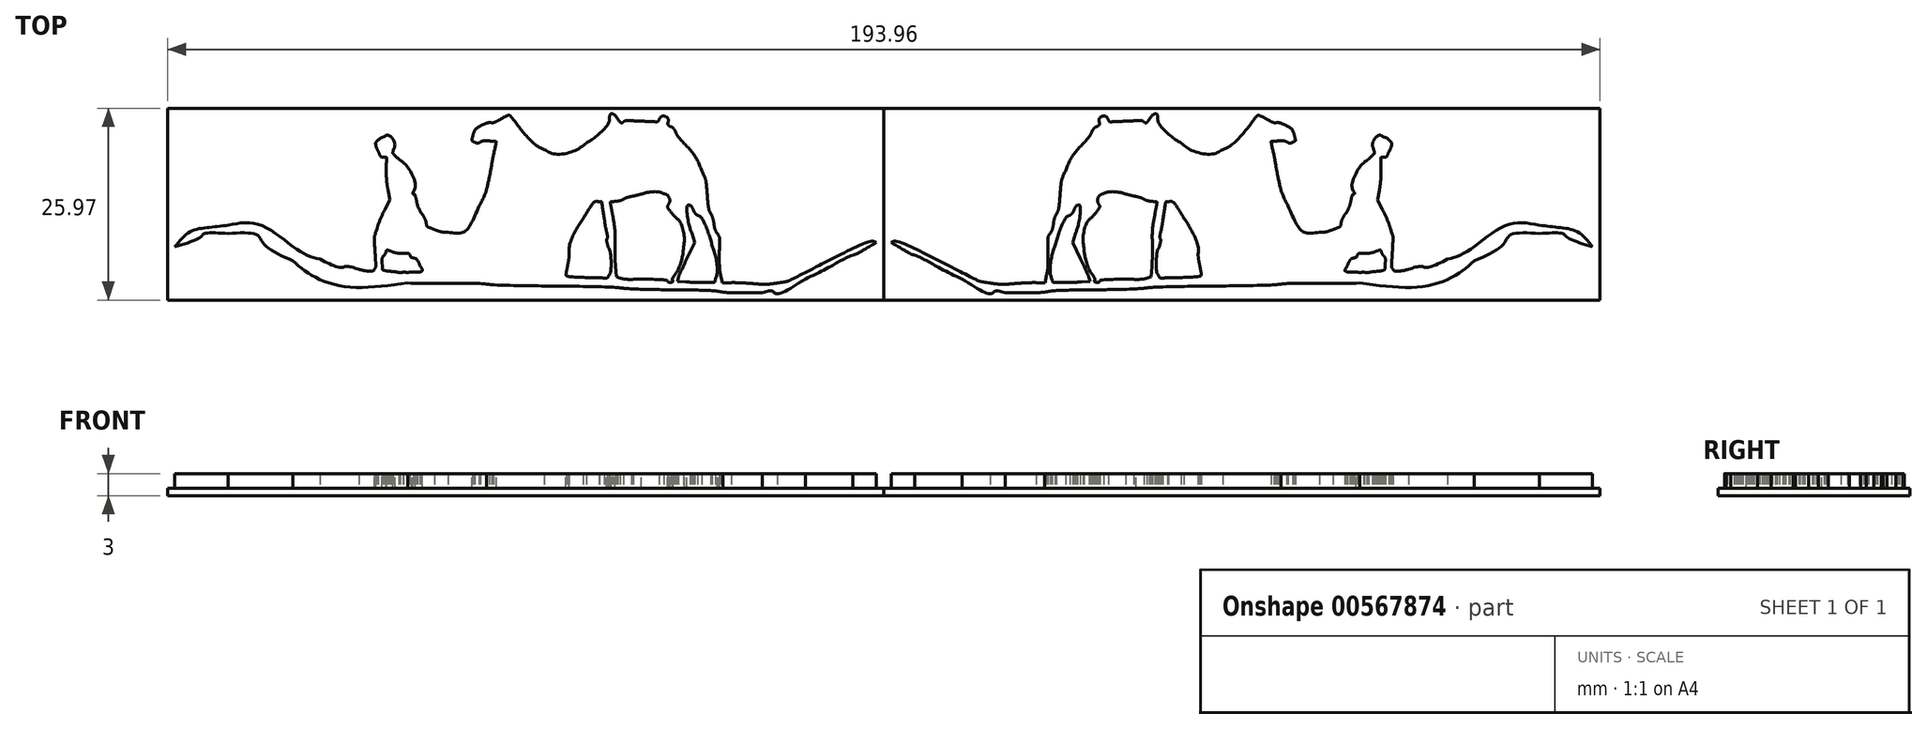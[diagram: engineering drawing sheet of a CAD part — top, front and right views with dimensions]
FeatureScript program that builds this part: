
annotation { "Feature Type Name" : "Feature", "Feature Type Description" : "" }
export const myFeature = defineFeature(function(context is Context, id is Id, definition is map)
    precondition{}
    {
        {
            var Q0;
            Q0=qCreatedBy(makeId("Top.planeOp"),FACE);
            var sketch = newSketch(context, id + "F0", { "sketchPlane" : qUnion([Q0])});
            skPoint(sketch, "E0.middle", {"position": v(0, 0) * mm});
            skFitSpline(sketch, "E1", {"points": [v(26.7, -11.93) * mm, v(25.66, -11.75) * mm, v(23.58, -11.65) * mm, v(20.02, -11.6) * mm]});
            skFitSpline(sketch, "E2", {"points": [v(20.02, -11.6) * mm, v(17.17, -11.57) * mm, v(14.02, -11.46) * mm, v(13, -11.36) * mm]});
            skFitSpline(sketch, "E3", {"points": [v(13, -11.36) * mm, v(12, -11.27) * mm, v(7.87, -11.15) * mm, v(3.83, -11.1) * mm]});
            skFitSpline(sketch, "E4", {"points": [v(3.83, -11.1) * mm, v(-0.2, -11.05) * mm, v(-4.31, -10.93) * mm, v(-5.3, -10.84) * mm]});
            skFitSpline(sketch, "E5", {"points": [v(-5.3, -10.84) * mm, v(-6.28, -10.75) * mm, v(-11.08, -10.75) * mm, v(-15.97, -10.7) * mm]});
            skFitSpline(sketch, "E6", {"points": [v(-15.97, -10.7) * mm, v(-24.16, -11.2) * mm, v(-28.99, -9.62) * mm, v(-31.48, -7.69) * mm]});
            skFitSpline(sketch, "E7", {"points": [v(-31.48, -7.69) * mm, v(-35.44, -5.43) * mm, v(-36.3, -4.22) * mm, v(-40.29, -4) * mm]});
            skFitSpline(sketch, "E8", {"points": [v(-40.29, -4) * mm, v(-43.5, -4.01) * mm, v(-44.02, -4.46) * mm, v(-47.5, -5.8) * mm]});
            skFitSpline(sketch, "E9", {"points": [v(-47.5, -5.8) * mm, v(-45.49, -3.77) * mm, v(-43.1, -3.18) * mm, v(-40.24, -2.86) * mm]});
            skFitSpline(sketch, "E10", {"points": [v(-40.24, -2.86) * mm, v(-35.9, -2.82) * mm, v(-30.7, -6.32) * mm, v(-27.85, -7.45) * mm]});
            skFitSpline(sketch, "E11", {"points": [v(-27.85, -7.45) * mm, v(-25.01, -8.6) * mm, v(-24.29, -8.43) * mm, v(-22.55, -8.84) * mm]});
            skFitSpline(sketch, "E12", {"points": [v(-22.55, -8.84) * mm, v(-22.19, -8.93) * mm, v(-20.69, -9.05) * mm, v(-20.45, -8.77) * mm]});
            skFitSpline(sketch, "E13", {"points": [v(-20.45, -8.77) * mm, v(-20.31, -8.6) * mm, v(-20.29, -7.98) * mm, v(-20.37, -6.51) * mm]});
            skFitSpline(sketch, "E14", {"points": [v(-20.37, -6.51) * mm, v(-20.48, -4.67) * mm, v(-20.46, -4.39) * mm, v(-20.1, -3.3) * mm]});
            skFitSpline(sketch, "E15", {"points": [v(-20.1, -3.3) * mm, v(-19.9, -2.63) * mm, v(-19.42, -1.49) * mm, v(-19.05, -0.76) * mm]});
            skFitSpline(sketch, "E16", {"points": [v(-18.62, 1.91) * mm, v(-18.75, 2.65) * mm, v(-18.85, 3.95) * mm, v(-18.84, 4.8) * mm]});
            skFitSpline(sketch, "E17", {"points": [v(-18.84, 4.8) * mm, v(-18.83, 6.29) * mm, v(-18.84, 6.34) * mm, v(-19.2, 6.34) * mm]});
            skFitSpline(sketch, "E18", {"points": [v(-19.2, 6.34) * mm, v(-19.48, 6.34) * mm, v(-19.66, 6.53) * mm, v(-19.93, 7.09) * mm]});
            skFitSpline(sketch, "E19", {"points": [v(-19.93, 7.09) * mm, v(-20.12, 7.5) * mm, v(-20.28, 7.94) * mm, v(-20.28, 8.06) * mm]});
            skFitSpline(sketch, "E20", {"points": [v(-20.28, 8.06) * mm, v(-20.28, 8.32) * mm, v(-19.66, 8.91) * mm, v(-19.22, 9.07) * mm]});
            skFitSpline(sketch, "E21", {"points": [v(-19.22, 9.07) * mm, v(-18.52, 9.31) * mm, v(-17.71, 8.24) * mm, v(-17.9, 7.3) * mm]});
            skFitSpline(sketch, "E22", {"points": [v(-17.9, 7.3) * mm, v(-17.96, 6.93) * mm, v(-17.84, 6.73) * mm, v(-17.15, 6.1) * mm]});
            skFitSpline(sketch, "E23", {"points": [v(-17.15, 6.1) * mm, v(-15.99, 5.03) * mm, v(-14.9, 2.56) * mm, v(-15.2, 1.65) * mm]});
            skFitSpline(sketch, "E24", {"points": [v(-15.2, 1.65) * mm, v(-15.25, 1.48) * mm, v(-15.22, 1.33) * mm, v(-15.13, 1.33) * mm]});
            skFitSpline(sketch, "E25", {"points": [v(-15.13, 1.33) * mm, v(-15.04, 1.33) * mm, v(-14.87, 0.91) * mm, v(-14.75, 0.4) * mm]});
            skFitSpline(sketch, "E26", {"points": [v(-14.75, 0.4) * mm, v(-14.64, -0.12) * mm, v(-14.32, -0.87) * mm, v(-14.05, -1.28) * mm]});
            skFitSpline(sketch, "E27", {"points": [v(-14.05, -1.28) * mm, v(-13.78, -1.7) * mm, v(-13.5, -2.26) * mm, v(-13.45, -2.54) * mm]});
            skFitSpline(sketch, "E28", {"points": [v(-13.45, -2.54) * mm, v(-13.36, -2.99) * mm, v(-13.2, -3.1) * mm, v(-12.35, -3.44) * mm]});
            skFitSpline(sketch, "E29", {"points": [v(-12.35, -3.44) * mm, v(-11.8, -3.65) * mm, v(-10.97, -3.83) * mm, v(-10.5, -3.83) * mm]});
            skFitSpline(sketch, "E30", {"points": [v(-10.5, -3.83) * mm, v(-8.53, -3.85) * mm, v(-7.65, -3.1) * mm, v(-6.27, -0.25) * mm]});
            skFitSpline(sketch, "E31", {"points": [v(-6.27, -0.25) * mm, v(-5.48, 1.37) * mm, v(-5.21, 2.24) * mm, v(-4.91, 3.65) * mm]});
            skFitSpline(sketch, "E32", {"points": [v(-4.91, 3.65) * mm, v(-4.7, 4.7) * mm, v(-4.46, 6.1) * mm, v(-4.33, 6.7) * mm]});
            skFitSpline(sketch, "E33", {"points": [v(-4.33, 6.7) * mm, v(-3.96, 8.44) * mm, v(-3.97, 8.46) * mm, v(-4.89, 8.55) * mm]});
            skFitSpline(sketch, "E34", {"points": [v(-4.89, 8.55) * mm, v(-5.33, 8.59) * mm, v(-5.86, 8.53) * mm, v(-6.09, 8.42) * mm]});
            skFitSpline(sketch, "E35", {"points": [v(-6.09, 8.42) * mm, v(-6.39, 8.27) * mm, v(-6.6, 8.26) * mm, v(-6.89, 8.4) * mm]});
            skFitSpline(sketch, "E36", {"points": [v(-6.89, 8.4) * mm, v(-7.21, 8.54) * mm, v(-7.26, 8.65) * mm, v(-7.17, 9.08) * mm]});
            skFitSpline(sketch, "E37", {"points": [v(-7.17, 9.08) * mm, v(-7.1, 9.36) * mm, v(-7, 9.7) * mm, v(-6.92, 9.85) * mm]});
            skFitSpline(sketch, "E38", {"points": [v(-6.92, 9.85) * mm, v(-6.76, 10.17) * mm, v(-5.08, 11.01) * mm, v(-4.6, 11.01) * mm]});
            skFitSpline(sketch, "E39", {"points": [v(-4.6, 11.01) * mm, v(-4.42, 11.01) * mm, v(-3.98, 11.16) * mm, v(-3.64, 11.34) * mm]});
            skFitSpline(sketch, "E40", {"points": [v(-3.64, 11.34) * mm, v(-2.3, 12.04) * mm, v(-2.12, 11.98) * mm, v(-1.03, 10.64) * mm]});
            skFitSpline(sketch, "E41", {"points": [v(-1.03, 10.64) * mm, v(0.14, 9.19) * mm, v(1.71, 7.77) * mm, v(2.56, 7.4) * mm]});
            skFitSpline(sketch, "E42", {"points": [v(2.56, 7.4) * mm, v(3.94, 6.79) * mm, v(6.6, 7.2) * mm, v(8.23, 8.27) * mm]});
            skFitSpline(sketch, "E43", {"points": [v(8.23, 8.27) * mm, v(9.44, 9.07) * mm, v(11.26, 10.96) * mm, v(11.37, 11.55) * mm]});
            skFitSpline(sketch, "E44", {"points": [v(11.37, 11.55) * mm, v(11.5, 12.17) * mm, v(11.95, 12.15) * mm, v(12.5, 11.48) * mm]});
            skFitSpline(sketch, "E45", {"points": [v(12.5, 11.48) * mm, v(12.88, 11.04) * mm, v(13, 10.98) * mm, v(13.25, 11.14) * mm]});
            skFitSpline(sketch, "E46", {"points": [v(13.25, 11.14) * mm, v(13.46, 11.26) * mm, v(14.25, 11.3) * mm, v(15.7, 11.23) * mm]});
            skFitSpline(sketch, "E47", {"points": [v(15.7, 11.23) * mm, v(17.57, 11.14) * mm, v(17.88, 11.17) * mm, v(18.08, 11.4) * mm]});
            skFitSpline(sketch, "E48", {"points": [v(18.08, 11.4) * mm, v(18.5, 11.91) * mm, v(19.27, 11.63) * mm, v(19.27, 10.97) * mm]});
            skFitSpline(sketch, "E49", {"points": [v(19.27, 10.97) * mm, v(19.27, 10.8) * mm, v(19.44, 10.59) * mm, v(19.66, 10.5) * mm]});
            skFitSpline(sketch, "E50", {"points": [v(19.66, 10.5) * mm, v(19.88, 10.4) * mm, v(20.18, 10.05) * mm, v(20.33, 9.73) * mm]});
            skFitSpline(sketch, "E51", {"points": [v(20.33, 9.73) * mm, v(20.48, 9.42) * mm, v(20.93, 8.8) * mm, v(21.32, 8.37) * mm]});
            skFitSpline(sketch, "E52", {"points": [v(21.32, 8.37) * mm, v(22.48, 7.11) * mm, v(23.25, 5.94) * mm, v(23.86, 4.53) * mm]});
            skFitSpline(sketch, "E53", {"points": [v(23.86, 4.53) * mm, v(24.34, 3.44) * mm, v(24.46, 2.89) * mm, v(24.6, 1.26) * mm]});
            skFitSpline(sketch, "E54", {"points": [v(24.6, 1.26) * mm, v(24.72, -0.01) * mm, v(24.88, -0.9) * mm, v(25.09, -1.3) * mm]});
            skFitSpline(sketch, "E55", {"points": [v(25.09, -1.3) * mm, v(25.26, -1.64) * mm, v(25.45, -2.26) * mm, v(25.5, -2.68) * mm]});
            skFitSpline(sketch, "E56", {"points": [v(25.5, -2.68) * mm, v(25.57, -3.1) * mm, v(25.76, -3.67) * mm, v(25.94, -3.97) * mm]});
            skFitSpline(sketch, "E57", {"points": [v(25.94, -3.97) * mm, v(26.22, -4.42) * mm, v(26.26, -4.79) * mm, v(26.24, -6.55) * mm]});
            skFitSpline(sketch, "E58", {"points": [v(26.24, -6.55) * mm, v(26.23, -7.67) * mm, v(26.32, -9.05) * mm, v(26.43, -9.61) * mm]});
            skLineSegment(sketch, "E59", {"start": v(-19.05, -0.76) * mm, "end": v(-18.39, 0.58) * mm});
            skLineSegment(sketch, "E60", {"start": v(-18.39, 0.58) * mm, "end": v(-18.62, 1.91) * mm});
            skFitSpline(sketch, "E61", {"points": [v(27.84, -10.64) * mm, v(28.5, -10.64) * mm, v(29.84, -10.7) * mm, v(30.83, -10.77) * mm]});
            skFitSpline(sketch, "E62", {"points": [v(30.83, -10.77) * mm, v(32.1, -10.86) * mm, v(33.06, -10.83) * mm, v(34.08, -10.67) * mm]});
            skFitSpline(sketch, "E63", {"points": [v(34.08, -10.67) * mm, v(35.42, -10.47) * mm, v(35.87, -10.28) * mm, v(39.72, -8.33) * mm]});
            skFitSpline(sketch, "E64", {"points": [v(39.72, -8.33) * mm, v(43.61, -6.35) * mm, v(46.93, -5.02) * mm, v(47.5, -5.21) * mm]});
            skFitSpline(sketch, "E65", {"points": [v(47.5, -5.21) * mm, v(45.59, -6.32) * mm, v(44.86, -6.73) * mm, v(44.3, -6.9) * mm]});
            skFitSpline(sketch, "E66", {"points": [v(44.3, -6.9) * mm, v(42.86, -7.57) * mm, v(41.25, -8.48) * mm, v(37.87, -10.16) * mm]});
            skFitSpline(sketch, "E67", {"points": [v(37.87, -10.16) * mm, v(33.93, -12.13) * mm, v(33.41, -11.77) * mm, v(32.05, -12) * mm]});
            skFitSpline(sketch, "E68", {"points": [v(32.05, -12) * mm, v(30.61, -12) * mm, v(27.7, -12) * mm, v(26.7, -11.93) * mm]});
            skLineSegment(sketch, "E69", {"start": v(26.43, -9.61) * mm, "end": v(26.64, -10.64) * mm});
            skLineSegment(sketch, "E70", {"start": v(26.64, -10.64) * mm, "end": v(27.84, -10.64) * mm});
            skFitSpline(sketch, "E71", {"points": [v(25.68, -10.26) * mm, v(25.94, -9.3) * mm, v(25.76, -7.18) * mm, v(25.29, -5.63) * mm]});
            skFitSpline(sketch, "E72", {"points": [v(25.29, -5.63) * mm, v(24.71, -3.77) * mm, v(23.74, -1.75) * mm, v(23.3, -1.52) * mm]});
            skFitSpline(sketch, "E73", {"points": [v(23.3, -1.52) * mm, v(23.12, -1.42) * mm, v(22.86, -1.08) * mm, v(22.7, -0.76) * mm]});
            skFitSpline(sketch, "E74", {"points": [v(22.7, -0.76) * mm, v(22.55, -0.43) * mm, v(22.35, -0.17) * mm, v(22.26, -0.17) * mm]});
            skFitSpline(sketch, "E75", {"points": [v(22.26, -0.17) * mm, v(21.93, -0.17) * mm, v(22.1, -2.62) * mm, v(22.5, -3.92) * mm]});
            skFitSpline(sketch, "E76", {"points": [v(21.85, -7.4) * mm, v(21.27, -8.6) * mm, v(20.74, -9.8) * mm, v(20.68, -10.05) * mm]});
            skLineSegment(sketch, "E77", {"start": v(22.5, -3.92) * mm, "end": v(22.9, -5.19) * mm});
            skLineSegment(sketch, "E78", {"start": v(22.9, -5.19) * mm, "end": v(21.85, -7.4) * mm});
            skFitSpline(sketch, "E79", {"points": [v(21.71, -10.55) * mm, v(22.34, -10.58) * mm, v(23.47, -10.6) * mm, v(24.22, -10.6) * mm]});
            skFitSpline(sketch, "E80", {"points": [v(24.22, -10.6) * mm, v(25.45, -10.6) * mm, v(25.6, -10.56) * mm, v(25.68, -10.26) * mm]});
            skLineSegment(sketch, "E81", {"start": v(20.68, -10.05) * mm, "end": v(20.57, -10.5) * mm});
            skLineSegment(sketch, "E82", {"start": v(20.57, -10.5) * mm, "end": v(21.71, -10.55) * mm});
            skFitSpline(sketch, "E83", {"points": [v(19.9, -10.3) * mm, v(19.88, -10.19) * mm, v(20, -9.9) * mm, v(20.16, -9.65) * mm]});
            skFitSpline(sketch, "E84", {"points": [v(20.16, -9.65) * mm, v(20.62, -8.95) * mm, v(21.26, -6.98) * mm, v(21.37, -5.9) * mm]});
            skFitSpline(sketch, "E85", {"points": [v(21.37, -5.9) * mm, v(21.5, -4.65) * mm, v(20.97, -2.5) * mm, v(20.4, -1.86) * mm]});
            skFitSpline(sketch, "E86", {"points": [v(20.4, -1.86) * mm, v(19.68, -1.09) * mm, v(19.23, -0.33) * mm, v(19.33, -0.08) * mm]});
            skFitSpline(sketch, "E87", {"points": [v(19.33, -0.08) * mm, v(19.54, 0.47) * mm, v(19.23, 1.2) * mm, v(18.7, 1.41) * mm]});
            skFitSpline(sketch, "E88", {"points": [v(18.7, 1.41) * mm, v(18.12, 1.64) * mm, v(16.69, 1.62) * mm, v(15.68, 1.35) * mm]});
            skFitSpline(sketch, "E89", {"points": [v(15.68, 1.35) * mm, v(15.31, 1.26) * mm, v(14.71, 1.12) * mm, v(14.34, 1.04) * mm]});
            skFitSpline(sketch, "E90", {"points": [v(14.34, 1.04) * mm, v(13.98, 0.96) * mm, v(13.5, 0.8) * mm, v(13.26, 0.67) * mm]});
            skFitSpline(sketch, "E91", {"points": [v(13.26, 0.67) * mm, v(13.04, 0.55) * mm, v(12.55, 0.41) * mm, v(12.18, 0.37) * mm]});
            skFitSpline(sketch, "E92", {"points": [v(12.18, 0.37) * mm, v(11.81, 0.33) * mm, v(11.5, 0.29) * mm, v(11.5, 0.27) * mm]});
            skFitSpline(sketch, "E93", {"points": [v(11.5, 0.27) * mm, v(11.48, 0.26) * mm, v(11.63, -0.58) * mm, v(11.8, -1.59) * mm]});
            skFitSpline(sketch, "E94", {"points": [v(11.8, -1.59) * mm, v(12.01, -2.77) * mm, v(12.12, -4.08) * mm, v(12.1, -5.26) * mm]});
            skFitSpline(sketch, "E95", {"points": [v(12.1, -5.26) * mm, v(12.1, -6.27) * mm, v(12.13, -7.7) * mm, v(12.19, -8.46) * mm]});
            skFitSpline(sketch, "E96", {"points": [v(12.85, -10.01) * mm, v(13.15, -10.11) * mm, v(13.95, -10.2) * mm, v(14.62, -10.2) * mm]});
            skFitSpline(sketch, "E97", {"points": [v(14.62, -10.2) * mm, v(16.29, -10.18) * mm, v(19.14, -10.33) * mm, v(19.24, -10.43) * mm]});
            skFitSpline(sketch, "E98", {"points": [v(19.24, -10.43) * mm, v(19.41, -10.6) * mm, v(19.95, -10.5) * mm, v(19.9, -10.3) * mm]});
            skLineSegment(sketch, "E99", {"start": v(12.19, -8.46) * mm, "end": v(12.29, -9.83) * mm});
            skLineSegment(sketch, "E100", {"start": v(12.29, -9.83) * mm, "end": v(12.85, -10.01) * mm});
            skFitSpline(sketch, "E101", {"points": [v(11.25, -9.69) * mm, v(11.5, -9.21) * mm, v(11.47, -6.48) * mm, v(11.2, -5.82) * mm]});
            skFitSpline(sketch, "E102", {"points": [v(11.2, -5.82) * mm, v(10.98, -4.84) * mm, v(11.02, -4.75) * mm, v(11.04, -4.68) * mm]});
            skFitSpline(sketch, "E103", {"points": [v(11.04, -4.68) * mm, v(11.12, -4.4) * mm, v(11.11, -4.4) * mm, v(11.08, -4.23) * mm]});
            skFitSpline(sketch, "E104", {"points": [v(11.08, -4.23) * mm, v(11.05, -4.06) * mm, v(10.83, -3.1) * mm, v(10.68, -2.09) * mm]});
            skFitSpline(sketch, "E105", {"points": [v(10.68, -2.09) * mm, v(10.34, 0.21) * mm, v(10.3, 0.33) * mm, v(9.93, 0.33) * mm]});
            skFitSpline(sketch, "E106", {"points": [v(9.93, 0.33) * mm, v(9.4, 0.33) * mm, v(8.85, -0.26) * mm, v(7.8, -1.95) * mm]});
            skFitSpline(sketch, "E107", {"points": [v(7.8, -1.95) * mm, v(6.75, -3.64) * mm, v(5.92, -5.73) * mm, v(5.91, -6.7) * mm]});
            skFitSpline(sketch, "E108", {"points": [v(5.91, -6.7) * mm, v(5.9, -7) * mm, v(5.8, -7.78) * mm, v(5.68, -8.43) * mm]});
            skFitSpline(sketch, "E109", {"points": [v(5.68, -8.43) * mm, v(5.55, -9.07) * mm, v(5.48, -9.63) * mm, v(5.52, -9.67) * mm]});
            skFitSpline(sketch, "E110", {"points": [v(5.52, -9.67) * mm, v(5.6, -9.75) * mm, v(8.38, -9.94) * mm, v(10.04, -9.99) * mm]});
            skFitSpline(sketch, "E111", {"points": [v(10.04, -9.99) * mm, v(10.91, -10) * mm, v(11.1, -9.96) * mm, v(11.25, -9.69) * mm]});
            skFitSpline(sketch, "E112", {"points": [v(0.74, -9.57) * mm, v(1.15, -9.6) * mm, v(1.58, -9.58) * mm, v(2.7, -9.62) * mm]});
            skFitSpline(sketch, "E113", {"points": [v(4.84, -9.06) * mm, v(4.9, -8.71) * mm, v(5.05, -7.9) * mm, v(5.19, -7.27) * mm]});
            skFitSpline(sketch, "E114", {"points": [v(5.19, -7.27) * mm, v(5.34, -6.54) * mm, v(5.4, -5.8) * mm, v(5.33, -5.24) * mm]});
            skFitSpline(sketch, "E115", {"points": [v(5.33, -5.24) * mm, v(5.2, -4.3) * mm, v(5.18, -4.36) * mm, v(6.4, -2.17) * mm]});
            skFitSpline(sketch, "E116", {"points": [v(6.4, -2.17) * mm, v(6.8, -1.48) * mm, v(7.26, -0.47) * mm, v(7.44, 0.07) * mm]});
            skFitSpline(sketch, "E117", {"points": [v(7.44, 0.07) * mm, v(7.76, 1.02) * mm, v(7.77, 1.09) * mm, v(7.5, 1.8) * mm]});
            skFitSpline(sketch, "E118", {"points": [v(7.5, 1.8) * mm, v(7.16, 2.67) * mm, v(6.43, 3.5) * mm, v(6, 3.5) * mm]});
            skFitSpline(sketch, "E119", {"points": [v(6, 3.5) * mm, v(5.33, 3.5) * mm, v(2.98, 4.07) * mm, v(2.18, 4.42) * mm]});
            skFitSpline(sketch, "E120", {"points": [v(2.18, 4.42) * mm, v(1.33, 4.8) * mm, v(0.1, 5.72) * mm, v(-1.5, 7.2) * mm]});
            skFitSpline(sketch, "E121", {"points": [v(-1.5, 7.2) * mm, v(-1.97, 7.63) * mm, v(-2.65, 8.16) * mm, v(-3.05, 8.23) * mm]});
            skFitSpline(sketch, "E122", {"points": [v(-3.05, 8.23) * mm, v(-3.31, 8.27) * mm, v(-3.27, 8.2) * mm, v(-3.57, 6.6) * mm]});
            skFitSpline(sketch, "E123", {"points": [v(-3.57, 6.6) * mm, v(-4.3, 2.7) * mm, v(-4.8, 1.08) * mm, v(-5.7, -0.73) * mm]});
            skFitSpline(sketch, "E124", {"points": [v(-5.7, -0.73) * mm, v(-6.25, -1.87) * mm, v(-7.06, -3.25) * mm, v(-7.5, -3.57) * mm]});
            skFitSpline(sketch, "E125", {"points": [v(-7.5, -3.57) * mm, v(-8.01, -4.03) * mm, v(-8.87, -4.46) * mm, v(-9.48, -4.54) * mm]});
            skFitSpline(sketch, "E126", {"points": [v(-9.48, -4.54) * mm, v(-10.05, -4.71) * mm, v(-11.8, -4.36) * mm, v(-12.09, -4.31) * mm]});
            skFitSpline(sketch, "E127", {"points": [v(-12.09, -4.31) * mm, v(-12.85, -4.14) * mm, v(-12.68, -4.7) * mm, v(-12.47, -4.95) * mm]});
            skFitSpline(sketch, "E128", {"points": [v(-12.47, -4.95) * mm, v(-12.02, -5.07) * mm, v(-11.7, -5.65) * mm, v(-11.94, -5.93) * mm]});
            skFitSpline(sketch, "E129", {"points": [v(-11.94, -5.93) * mm, v(-12.08, -6.1) * mm, v(-12.08, -6.25) * mm, v(-11.93, -6.51) * mm]});
            skFitSpline(sketch, "E130", {"points": [v(-11.93, -6.51) * mm, v(-11.52, -7.3) * mm, v(-12.2, -7.6) * mm, v(-13.12, -7.06) * mm]});
            skFitSpline(sketch, "E131", {"points": [v(-13.12, -7.06) * mm, v(-13.58, -6.79) * mm, v(-13.62, -6.79) * mm, v(-13.89, -7.05) * mm]});
            skFitSpline(sketch, "E132", {"points": [v(-13.89, -7.05) * mm, v(-13.97, -7.24) * mm, v(-13.95, -7.4) * mm, v(-13.9, -7.53) * mm]});
            skFitSpline(sketch, "E133", {"points": [v(-13.9, -7.53) * mm, v(-13.75, -7.86) * mm, v(-13.47, -8.1) * mm, v(-13.2, -8.45) * mm]});
            skFitSpline(sketch, "E134", {"points": [v(-13.2, -8.45) * mm, v(-12.86, -8.97) * mm, v(-12.6, -9.17) * mm, v(-12.16, -9.25) * mm]});
            skFitSpline(sketch, "E135", {"points": [v(-12.16, -9.25) * mm, v(-11.84, -9.32) * mm, v(-9.1, -9.4) * mm, v(-6.05, -9.44) * mm]});
            skFitSpline(sketch, "E136", {"points": [v(-6.05, -9.44) * mm, v(-3.02, -9.48) * mm, v(-0.7, -9.52) * mm, v(-0.46, -9.55) * mm]});
            skFitSpline(sketch, "E137", {"points": [v(-0.46, -9.55) * mm, v(-0.08, -9.58) * mm, v(0.25, -9.55) * mm, v(0.74, -9.57) * mm]});
            skLineSegment(sketch, "E138", {"start": v(2.7, -9.62) * mm, "end": v(4.73, -9.7) * mm});
            skLineSegment(sketch, "E139", {"start": v(4.73, -9.7) * mm, "end": v(4.84, -9.06) * mm});
            skFitSpline(sketch, "E140", {"points": [v(-15.47, -9.21) * mm, v(-14.13, -9.14) * mm, v(-13.96, -8.97) * mm, v(-14.3, -8.34) * mm]});
            skFitSpline(sketch, "E141", {"points": [v(-14.3, -8.34) * mm, v(-14.35, -8.21) * mm, v(-14.43, -7.99) * mm, v(-14.61, -7.64) * mm]});
            skFitSpline(sketch, "E142", {"points": [v(-14.61, -7.64) * mm, v(-14.75, -7.46) * mm, v(-14.83, -7.4) * mm, v(-15.02, -7.34) * mm]});
            skFitSpline(sketch, "E143", {"points": [v(-15.02, -7.34) * mm, v(-15.25, -7.27) * mm, v(-15.5, -7.2) * mm, v(-15.6, -7) * mm]});
            skFitSpline(sketch, "E144", {"points": [v(-15.6, -7) * mm, v(-15.75, -6.75) * mm, v(-15.96, -6.68) * mm, v(-16.6, -6.68) * mm]});
            skFitSpline(sketch, "E145", {"points": [v(-16.6, -6.68) * mm, v(-17.04, -6.68) * mm, v(-17.71, -6.56) * mm, v(-18.1, -6.43) * mm]});
            skFitSpline(sketch, "E146", {"points": [v(-18.1, -6.43) * mm, v(-18.73, -6.2) * mm, v(-18.8, -6.2) * mm, v(-18.9, -6.47) * mm]});
            skFitSpline(sketch, "E147", {"points": [v(-18.9, -6.47) * mm, v(-18.95, -6.63) * mm, v(-19.1, -6.88) * mm, v(-19.23, -7.03) * mm]});
            skFitSpline(sketch, "E148", {"points": [v(-19.23, -7.03) * mm, v(-19.38, -7.2) * mm, v(-19.44, -7.6) * mm, v(-19.41, -8.1) * mm]});
            skFitSpline(sketch, "E149", {"points": [v(-19.41, -8.1) * mm, v(-19.37, -8.83) * mm, v(-19.31, -8.92) * mm, v(-18.89, -9.03) * mm]});
            skFitSpline(sketch, "E150", {"points": [v(-18.89, -9.03) * mm, v(-18.62, -9.1) * mm, v(-18.32, -9.1) * mm, v(-18.12, -9.12) * mm]});
            skFitSpline(sketch, "E151", {"points": [v(-18.12, -9.12) * mm, v(-17.67, -9.16) * mm, v(-17.26, -9.24) * mm, v(-16.94, -9.26) * mm]});
            skFitSpline(sketch, "E152", {"points": [v(-16.94, -9.26) * mm, v(-16.76, -9.26) * mm, v(-16.68, -9.24) * mm, v(-16.5, -9.24) * mm]});
            skFitSpline(sketch, "E153", {"points": [v(-16.5, -9.24) * mm, v(-16.32, -9.22) * mm, v(-16.14, -9.25) * mm, v(-15.47, -9.21) * mm]});
            skLineSegment(sketch, "E154", {"start": v(-15.47, -9.21) * mm, "end": v(-15.47, -9.21) * mm});
            skSolve(sketch);
        }
        {
            var Q0;
            Q0=makeQuery(id+"F0.imprint","IMPRINT",FACE,{"disambiguationData":[TD([[makeQuery(id+"F0.imprint","IMPRINT",EDGE,{"derivedFrom":sQuery(id+"F0.wireOp",EDGE,"E1")}),-1.0]])]});
            extrude(context, id + "F1", {"entities" : qUnion([Q0]), "depth" : 2 * mm, "offsetDistance" : 25 * mm});
        }
        {
            var Q0;
            Q0=makeQuery(id+"F1.opExtrude","CAP_FACE",FACE,{"disambiguationData":[OSD([sQuery(id+"F0.wireOp",EDGE,"E1"),sQuery(id+"F0.wireOp",EDGE,"E2"),sQuery(id+"F0.wireOp",EDGE,"E3"),sQuery(id+"F0.wireOp",EDGE,"E4"),sQuery(id+"F0.wireOp",EDGE,"E5"),sQuery(id+"F0.wireOp",EDGE,"E6"),sQuery(id+"F0.wireOp",EDGE,"E7"),sQuery(id+"F0.wireOp",EDGE,"E8"),sQuery(id+"F0.wireOp",EDGE,"E9"),sQuery(id+"F0.wireOp",EDGE,"E10"),sQuery(id+"F0.wireOp",EDGE,"E11"),sQuery(id+"F0.wireOp",EDGE,"E12"),sQuery(id+"F0.wireOp",EDGE,"E13"),sQuery(id+"F0.wireOp",EDGE,"E14"),sQuery(id+"F0.wireOp",EDGE,"E15"),sQuery(id+"F0.wireOp",EDGE,"E16"),sQuery(id+"F0.wireOp",EDGE,"E17"),sQuery(id+"F0.wireOp",EDGE,"E18"),sQuery(id+"F0.wireOp",EDGE,"E19"),sQuery(id+"F0.wireOp",EDGE,"E20"),sQuery(id+"F0.wireOp",EDGE,"E21"),sQuery(id+"F0.wireOp",EDGE,"E22"),sQuery(id+"F0.wireOp",EDGE,"E23"),sQuery(id+"F0.wireOp",EDGE,"E24"),sQuery(id+"F0.wireOp",EDGE,"E25"),sQuery(id+"F0.wireOp",EDGE,"E26"),sQuery(id+"F0.wireOp",EDGE,"E27"),sQuery(id+"F0.wireOp",EDGE,"E28"),sQuery(id+"F0.wireOp",EDGE,"E29"),sQuery(id+"F0.wireOp",EDGE,"E30"),sQuery(id+"F0.wireOp",EDGE,"E31"),sQuery(id+"F0.wireOp",EDGE,"E32"),sQuery(id+"F0.wireOp",EDGE,"E33"),sQuery(id+"F0.wireOp",EDGE,"E34"),sQuery(id+"F0.wireOp",EDGE,"E35"),sQuery(id+"F0.wireOp",EDGE,"E36"),sQuery(id+"F0.wireOp",EDGE,"E37"),sQuery(id+"F0.wireOp",EDGE,"E38"),sQuery(id+"F0.wireOp",EDGE,"E39"),sQuery(id+"F0.wireOp",EDGE,"E40"),sQuery(id+"F0.wireOp",EDGE,"E41"),sQuery(id+"F0.wireOp",EDGE,"E42"),sQuery(id+"F0.wireOp",EDGE,"E43"),sQuery(id+"F0.wireOp",EDGE,"E44"),sQuery(id+"F0.wireOp",EDGE,"E45"),sQuery(id+"F0.wireOp",EDGE,"E46"),sQuery(id+"F0.wireOp",EDGE,"E47"),sQuery(id+"F0.wireOp",EDGE,"E48"),sQuery(id+"F0.wireOp",EDGE,"E49"),sQuery(id+"F0.wireOp",EDGE,"E50"),sQuery(id+"F0.wireOp",EDGE,"E51"),sQuery(id+"F0.wireOp",EDGE,"E52"),sQuery(id+"F0.wireOp",EDGE,"E53"),sQuery(id+"F0.wireOp",EDGE,"E54"),sQuery(id+"F0.wireOp",EDGE,"E55"),sQuery(id+"F0.wireOp",EDGE,"E56"),sQuery(id+"F0.wireOp",EDGE,"E57"),sQuery(id+"F0.wireOp",EDGE,"E58"),sQuery(id+"F0.wireOp",EDGE,"E59"),sQuery(id+"F0.wireOp",EDGE,"E60"),sQuery(id+"F0.wireOp",EDGE,"E61"),sQuery(id+"F0.wireOp",EDGE,"E62"),sQuery(id+"F0.wireOp",EDGE,"E63"),sQuery(id+"F0.wireOp",EDGE,"E64"),sQuery(id+"F0.wireOp",EDGE,"E65"),sQuery(id+"F0.wireOp",EDGE,"E66"),sQuery(id+"F0.wireOp",EDGE,"E67"),sQuery(id+"F0.wireOp",EDGE,"E68"),sQuery(id+"F0.wireOp",EDGE,"E69"),sQuery(id+"F0.wireOp",EDGE,"E70"),sQuery(id+"F0.wireOp",EDGE,"E71"),sQuery(id+"F0.wireOp",EDGE,"E72"),sQuery(id+"F0.wireOp",EDGE,"E73"),sQuery(id+"F0.wireOp",EDGE,"E74"),sQuery(id+"F0.wireOp",EDGE,"E75"),sQuery(id+"F0.wireOp",EDGE,"E76"),sQuery(id+"F0.wireOp",EDGE,"E77"),sQuery(id+"F0.wireOp",EDGE,"E78"),sQuery(id+"F0.wireOp",EDGE,"E79"),sQuery(id+"F0.wireOp",EDGE,"E80"),sQuery(id+"F0.wireOp",EDGE,"E81"),sQuery(id+"F0.wireOp",EDGE,"E82"),sQuery(id+"F0.wireOp",EDGE,"E83"),sQuery(id+"F0.wireOp",EDGE,"E84"),sQuery(id+"F0.wireOp",EDGE,"E85"),sQuery(id+"F0.wireOp",EDGE,"E86"),sQuery(id+"F0.wireOp",EDGE,"E87"),sQuery(id+"F0.wireOp",EDGE,"E88"),sQuery(id+"F0.wireOp",EDGE,"E89"),sQuery(id+"F0.wireOp",EDGE,"E90"),sQuery(id+"F0.wireOp",EDGE,"E91"),sQuery(id+"F0.wireOp",EDGE,"E92"),sQuery(id+"F0.wireOp",EDGE,"E93"),sQuery(id+"F0.wireOp",EDGE,"E94"),sQuery(id+"F0.wireOp",EDGE,"E95"),sQuery(id+"F0.wireOp",EDGE,"E96"),sQuery(id+"F0.wireOp",EDGE,"E97"),sQuery(id+"F0.wireOp",EDGE,"E98"),sQuery(id+"F0.wireOp",EDGE,"E99"),sQuery(id+"F0.wireOp",EDGE,"E100"),sQuery(id+"F0.wireOp",EDGE,"E101"),sQuery(id+"F0.wireOp",EDGE,"E102"),sQuery(id+"F0.wireOp",EDGE,"E103"),sQuery(id+"F0.wireOp",EDGE,"E104"),sQuery(id+"F0.wireOp",EDGE,"E105"),sQuery(id+"F0.wireOp",EDGE,"E106"),sQuery(id+"F0.wireOp",EDGE,"E107"),sQuery(id+"F0.wireOp",EDGE,"E108"),sQuery(id+"F0.wireOp",EDGE,"E109"),sQuery(id+"F0.wireOp",EDGE,"E110"),sQuery(id+"F0.wireOp",EDGE,"E111"),sQuery(id+"F0.wireOp",EDGE,"E112"),sQuery(id+"F0.wireOp",EDGE,"E113"),sQuery(id+"F0.wireOp",EDGE,"E114"),sQuery(id+"F0.wireOp",EDGE,"E115"),sQuery(id+"F0.wireOp",EDGE,"E116"),sQuery(id+"F0.wireOp",EDGE,"E117"),sQuery(id+"F0.wireOp",EDGE,"E118"),sQuery(id+"F0.wireOp",EDGE,"E119"),sQuery(id+"F0.wireOp",EDGE,"E120"),sQuery(id+"F0.wireOp",EDGE,"E121"),sQuery(id+"F0.wireOp",EDGE,"E122"),sQuery(id+"F0.wireOp",EDGE,"E123"),sQuery(id+"F0.wireOp",EDGE,"E124"),sQuery(id+"F0.wireOp",EDGE,"E125"),sQuery(id+"F0.wireOp",EDGE,"E126"),sQuery(id+"F0.wireOp",EDGE,"E127"),sQuery(id+"F0.wireOp",EDGE,"E128"),sQuery(id+"F0.wireOp",EDGE,"E129"),sQuery(id+"F0.wireOp",EDGE,"E130"),sQuery(id+"F0.wireOp",EDGE,"E131"),sQuery(id+"F0.wireOp",EDGE,"E132"),sQuery(id+"F0.wireOp",EDGE,"E133"),sQuery(id+"F0.wireOp",EDGE,"E134"),sQuery(id+"F0.wireOp",EDGE,"E135"),sQuery(id+"F0.wireOp",EDGE,"E136"),sQuery(id+"F0.wireOp",EDGE,"E137"),sQuery(id+"F0.wireOp",EDGE,"E138"),sQuery(id+"F0.wireOp",EDGE,"E139"),sQuery(id+"F0.wireOp",EDGE,"E140"),sQuery(id+"F0.wireOp",EDGE,"E141"),sQuery(id+"F0.wireOp",EDGE,"E142"),sQuery(id+"F0.wireOp",EDGE,"E143"),sQuery(id+"F0.wireOp",EDGE,"E144"),sQuery(id+"F0.wireOp",EDGE,"E145"),sQuery(id+"F0.wireOp",EDGE,"E146"),sQuery(id+"F0.wireOp",EDGE,"E147"),sQuery(id+"F0.wireOp",EDGE,"E148"),sQuery(id+"F0.wireOp",EDGE,"E149"),sQuery(id+"F0.wireOp",EDGE,"E150"),sQuery(id+"F0.wireOp",EDGE,"E151"),sQuery(id+"F0.wireOp",EDGE,"E152"),sQuery(id+"F0.wireOp",EDGE,"E153")])],"isStart":true});
            var sketch = newSketch(context, id + "F2", { "sketchPlane" : qUnion([Q0])});
            skLineSegment(sketch, "E155.bottom", {"start": v(48.5, 13) * mm, "end": v(-48.5, 13) * mm});
            skLineSegment(sketch, "E155.top", {"start": v(48.5, -12.97) * mm, "end": v(-48.5, -12.97) * mm});
            skLineSegment(sketch, "E155.left", {"start": v(48.5, 13) * mm, "end": v(48.5, -12.97) * mm});
            skLineSegment(sketch, "E155.right", {"start": v(-48.5, 13) * mm, "end": v(-48.5, -12.97) * mm});
            skSolve(sketch);
        }
        {
            var Q0;
            Q0=qSketchRegion(id+"F2",true);
            extrude(context, id + "F3", {"entities" : qUnion([Q0]), "operationType" : NewBodyOperationType.ADD, "depth" : 1 * mm, "offsetDistance" : 25 * mm});
        }
        {
            var Q0;
            Q0=makeQuery(id+"F1.opExtrude","SWEPT_BODY",BODY,{"disambiguationData":[OSD([sQuery(id+"F0.wireOp",EDGE,"E1"),sQuery(id+"F0.wireOp",EDGE,"E2"),sQuery(id+"F0.wireOp",EDGE,"E3"),sQuery(id+"F0.wireOp",EDGE,"E4"),sQuery(id+"F0.wireOp",EDGE,"E5"),sQuery(id+"F0.wireOp",EDGE,"E6"),sQuery(id+"F0.wireOp",EDGE,"E7"),sQuery(id+"F0.wireOp",EDGE,"E8"),sQuery(id+"F0.wireOp",EDGE,"E9"),sQuery(id+"F0.wireOp",EDGE,"E10"),sQuery(id+"F0.wireOp",EDGE,"E11"),sQuery(id+"F0.wireOp",EDGE,"E12"),sQuery(id+"F0.wireOp",EDGE,"E13"),sQuery(id+"F0.wireOp",EDGE,"E14"),sQuery(id+"F0.wireOp",EDGE,"E15"),sQuery(id+"F0.wireOp",EDGE,"E16"),sQuery(id+"F0.wireOp",EDGE,"E17"),sQuery(id+"F0.wireOp",EDGE,"E18"),sQuery(id+"F0.wireOp",EDGE,"E19"),sQuery(id+"F0.wireOp",EDGE,"E20"),sQuery(id+"F0.wireOp",EDGE,"E21"),sQuery(id+"F0.wireOp",EDGE,"E22"),sQuery(id+"F0.wireOp",EDGE,"E23"),sQuery(id+"F0.wireOp",EDGE,"E24"),sQuery(id+"F0.wireOp",EDGE,"E25"),sQuery(id+"F0.wireOp",EDGE,"E26"),sQuery(id+"F0.wireOp",EDGE,"E27"),sQuery(id+"F0.wireOp",EDGE,"E28"),sQuery(id+"F0.wireOp",EDGE,"E29"),sQuery(id+"F0.wireOp",EDGE,"E30"),sQuery(id+"F0.wireOp",EDGE,"E31"),sQuery(id+"F0.wireOp",EDGE,"E32"),sQuery(id+"F0.wireOp",EDGE,"E33"),sQuery(id+"F0.wireOp",EDGE,"E34"),sQuery(id+"F0.wireOp",EDGE,"E35"),sQuery(id+"F0.wireOp",EDGE,"E36"),sQuery(id+"F0.wireOp",EDGE,"E37"),sQuery(id+"F0.wireOp",EDGE,"E38"),sQuery(id+"F0.wireOp",EDGE,"E39"),sQuery(id+"F0.wireOp",EDGE,"E40"),sQuery(id+"F0.wireOp",EDGE,"E41"),sQuery(id+"F0.wireOp",EDGE,"E42"),sQuery(id+"F0.wireOp",EDGE,"E43"),sQuery(id+"F0.wireOp",EDGE,"E44"),sQuery(id+"F0.wireOp",EDGE,"E45"),sQuery(id+"F0.wireOp",EDGE,"E46"),sQuery(id+"F0.wireOp",EDGE,"E47"),sQuery(id+"F0.wireOp",EDGE,"E48"),sQuery(id+"F0.wireOp",EDGE,"E49"),sQuery(id+"F0.wireOp",EDGE,"E50"),sQuery(id+"F0.wireOp",EDGE,"E51"),sQuery(id+"F0.wireOp",EDGE,"E52"),sQuery(id+"F0.wireOp",EDGE,"E53"),sQuery(id+"F0.wireOp",EDGE,"E54"),sQuery(id+"F0.wireOp",EDGE,"E55"),sQuery(id+"F0.wireOp",EDGE,"E56"),sQuery(id+"F0.wireOp",EDGE,"E57"),sQuery(id+"F0.wireOp",EDGE,"E58"),sQuery(id+"F0.wireOp",EDGE,"E59"),sQuery(id+"F0.wireOp",EDGE,"E60"),sQuery(id+"F0.wireOp",EDGE,"E61"),sQuery(id+"F0.wireOp",EDGE,"E62"),sQuery(id+"F0.wireOp",EDGE,"E63"),sQuery(id+"F0.wireOp",EDGE,"E64"),sQuery(id+"F0.wireOp",EDGE,"E65"),sQuery(id+"F0.wireOp",EDGE,"E66"),sQuery(id+"F0.wireOp",EDGE,"E67"),sQuery(id+"F0.wireOp",EDGE,"E68"),sQuery(id+"F0.wireOp",EDGE,"E69"),sQuery(id+"F0.wireOp",EDGE,"E70"),sQuery(id+"F0.wireOp",EDGE,"E71"),sQuery(id+"F0.wireOp",EDGE,"E72"),sQuery(id+"F0.wireOp",EDGE,"E73"),sQuery(id+"F0.wireOp",EDGE,"E74"),sQuery(id+"F0.wireOp",EDGE,"E75"),sQuery(id+"F0.wireOp",EDGE,"E76"),sQuery(id+"F0.wireOp",EDGE,"E77"),sQuery(id+"F0.wireOp",EDGE,"E78"),sQuery(id+"F0.wireOp",EDGE,"E79"),sQuery(id+"F0.wireOp",EDGE,"E80"),sQuery(id+"F0.wireOp",EDGE,"E81"),sQuery(id+"F0.wireOp",EDGE,"E82"),sQuery(id+"F0.wireOp",EDGE,"E83"),sQuery(id+"F0.wireOp",EDGE,"E84"),sQuery(id+"F0.wireOp",EDGE,"E85"),sQuery(id+"F0.wireOp",EDGE,"E86"),sQuery(id+"F0.wireOp",EDGE,"E87"),sQuery(id+"F0.wireOp",EDGE,"E88"),sQuery(id+"F0.wireOp",EDGE,"E89"),sQuery(id+"F0.wireOp",EDGE,"E90"),sQuery(id+"F0.wireOp",EDGE,"E91"),sQuery(id+"F0.wireOp",EDGE,"E92"),sQuery(id+"F0.wireOp",EDGE,"E93"),sQuery(id+"F0.wireOp",EDGE,"E94"),sQuery(id+"F0.wireOp",EDGE,"E95"),sQuery(id+"F0.wireOp",EDGE,"E96"),sQuery(id+"F0.wireOp",EDGE,"E97"),sQuery(id+"F0.wireOp",EDGE,"E98"),sQuery(id+"F0.wireOp",EDGE,"E99"),sQuery(id+"F0.wireOp",EDGE,"E100"),sQuery(id+"F0.wireOp",EDGE,"E101"),sQuery(id+"F0.wireOp",EDGE,"E102"),sQuery(id+"F0.wireOp",EDGE,"E103"),sQuery(id+"F0.wireOp",EDGE,"E104"),sQuery(id+"F0.wireOp",EDGE,"E105"),sQuery(id+"F0.wireOp",EDGE,"E106"),sQuery(id+"F0.wireOp",EDGE,"E107"),sQuery(id+"F0.wireOp",EDGE,"E108"),sQuery(id+"F0.wireOp",EDGE,"E109"),sQuery(id+"F0.wireOp",EDGE,"E110"),sQuery(id+"F0.wireOp",EDGE,"E111"),sQuery(id+"F0.wireOp",EDGE,"E112"),sQuery(id+"F0.wireOp",EDGE,"E113"),sQuery(id+"F0.wireOp",EDGE,"E114"),sQuery(id+"F0.wireOp",EDGE,"E115"),sQuery(id+"F0.wireOp",EDGE,"E116"),sQuery(id+"F0.wireOp",EDGE,"E117"),sQuery(id+"F0.wireOp",EDGE,"E118"),sQuery(id+"F0.wireOp",EDGE,"E119"),sQuery(id+"F0.wireOp",EDGE,"E120"),sQuery(id+"F0.wireOp",EDGE,"E121"),sQuery(id+"F0.wireOp",EDGE,"E122"),sQuery(id+"F0.wireOp",EDGE,"E123"),sQuery(id+"F0.wireOp",EDGE,"E124"),sQuery(id+"F0.wireOp",EDGE,"E125"),sQuery(id+"F0.wireOp",EDGE,"E126"),sQuery(id+"F0.wireOp",EDGE,"E127"),sQuery(id+"F0.wireOp",EDGE,"E128"),sQuery(id+"F0.wireOp",EDGE,"E129"),sQuery(id+"F0.wireOp",EDGE,"E130"),sQuery(id+"F0.wireOp",EDGE,"E131"),sQuery(id+"F0.wireOp",EDGE,"E132"),sQuery(id+"F0.wireOp",EDGE,"E133"),sQuery(id+"F0.wireOp",EDGE,"E134"),sQuery(id+"F0.wireOp",EDGE,"E135"),sQuery(id+"F0.wireOp",EDGE,"E136"),sQuery(id+"F0.wireOp",EDGE,"E137"),sQuery(id+"F0.wireOp",EDGE,"E138"),sQuery(id+"F0.wireOp",EDGE,"E139"),sQuery(id+"F0.wireOp",EDGE,"E140"),sQuery(id+"F0.wireOp",EDGE,"E141"),sQuery(id+"F0.wireOp",EDGE,"E142"),sQuery(id+"F0.wireOp",EDGE,"E143"),sQuery(id+"F0.wireOp",EDGE,"E144"),sQuery(id+"F0.wireOp",EDGE,"E145"),sQuery(id+"F0.wireOp",EDGE,"E146"),sQuery(id+"F0.wireOp",EDGE,"E147"),sQuery(id+"F0.wireOp",EDGE,"E148"),sQuery(id+"F0.wireOp",EDGE,"E149"),sQuery(id+"F0.wireOp",EDGE,"E150"),sQuery(id+"F0.wireOp",EDGE,"E151"),sQuery(id+"F0.wireOp",EDGE,"E152"),sQuery(id+"F0.wireOp",EDGE,"E153")])]});
            var Q1;
            Q1=makeQuery(id+"F3.opExtrude","SWEPT_FACE",FACE,{"disambiguationData":[OSD([sQuery(id+"F2.wireOp",EDGE,"E155.left")])]});
            mirror(context, id + "F4", {"entities" : qUnion([Q0]), "mirrorPlane" : qUnion([Q1])});
        }
    });
